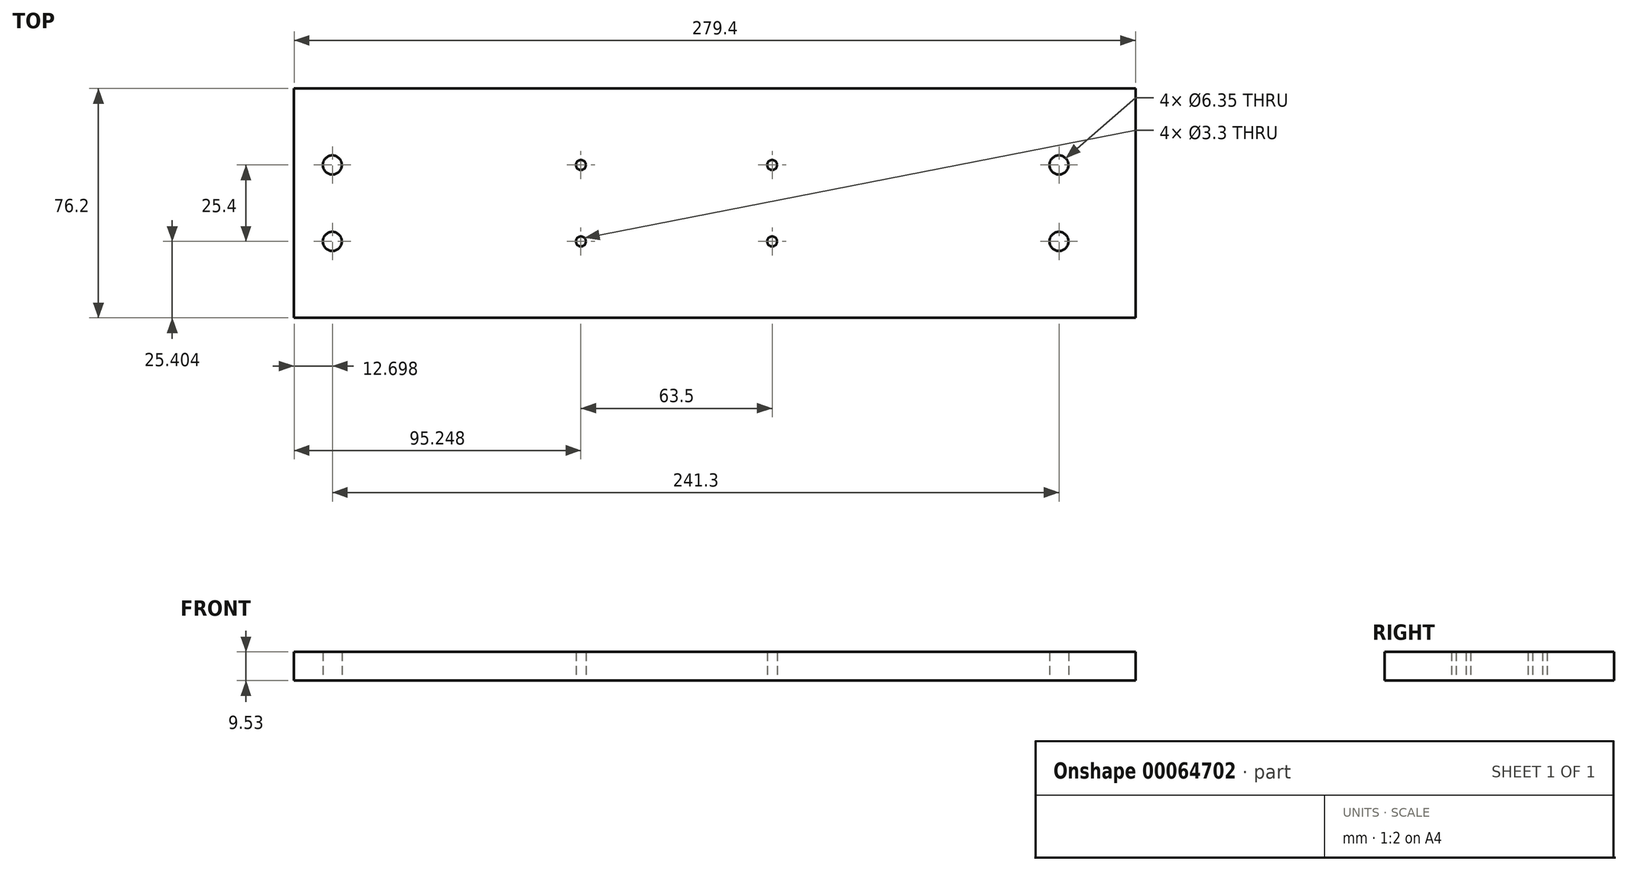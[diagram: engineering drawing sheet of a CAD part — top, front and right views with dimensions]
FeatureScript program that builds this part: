
annotation { "Feature Type Name" : "Feature", "Feature Type Description" : "" }
export const myFeature = defineFeature(function(context is Context, id is Id, definition is map)
    precondition{}
    {
        {
            var Q0;
            Q0=qCreatedBy(makeId("Top.planeOp"),FACE);
            var sketch = newSketch(context, id + "F0", { "sketchPlane" : qUnion([Q0])});
            skLineSegment(sketch, "E0.bottom", {"start": v(-134.28, 4.37) * mm, "end": v(145.12, 4.37) * mm});
            skLineSegment(sketch, "E0.top", {"start": v(-134.28, -71.83) * mm, "end": v(145.12, -71.83) * mm});
            skLineSegment(sketch, "E0.left", {"start": v(-134.28, 4.37) * mm, "end": v(-134.28, -71.83) * mm});
            skLineSegment(sketch, "E0.right", {"start": v(145.12, 4.37) * mm, "end": v(145.12, -71.83) * mm});
            skLineSegment(sketch, "E1", {"start": v(-146.23, -33.73) * mm, "end": v(154.98, -33.73) * mm, "construction": true});
            skLineSegment(sketch, "E2", {"start": v(-138.25, -21.03) * mm, "end": v(150.7, -21.03) * mm, "construction": true});
            skLineSegment(sketch, "E3", {"start": v(-142.24, -46.43) * mm, "end": v(150.7, -46.43) * mm, "construction": true});
            skCircle(sketch, "E4", {"center": v(-121.58, -21.03) * mm, "radius": 3.18 * mm});
            skCircle(sketch, "E5", {"center": v(-121.58, -46.43) * mm, "radius": 3.17 * mm});
            skCircle(sketch, "E6", {"center": v(-39.03, -21.03) * mm, "radius": 1.65 * mm});
            skCircle(sketch, "E7", {"center": v(-39.03, -46.43) * mm, "radius": 1.65 * mm});
            skCircle(sketch, "E8", {"center": v(24.47, -21.03) * mm, "radius": 1.65 * mm});
            skCircle(sketch, "E9", {"center": v(24.47, -46.43) * mm, "radius": 1.65 * mm});
            skCircle(sketch, "E10", {"center": v(119.72, -46.43) * mm, "radius": 3.18 * mm});
            skCircle(sketch, "E11", {"center": v(119.72, -21.03) * mm, "radius": 3.18 * mm});
            skSolve(sketch);
        }
        {
            var Q0;
            Q0 = qSketchRegion(id + "F0", true);
            extrude(context, id + "F1", {"entities" : qUnion([Q0]), "depth" : 9.52 * mm});
        }
    });
